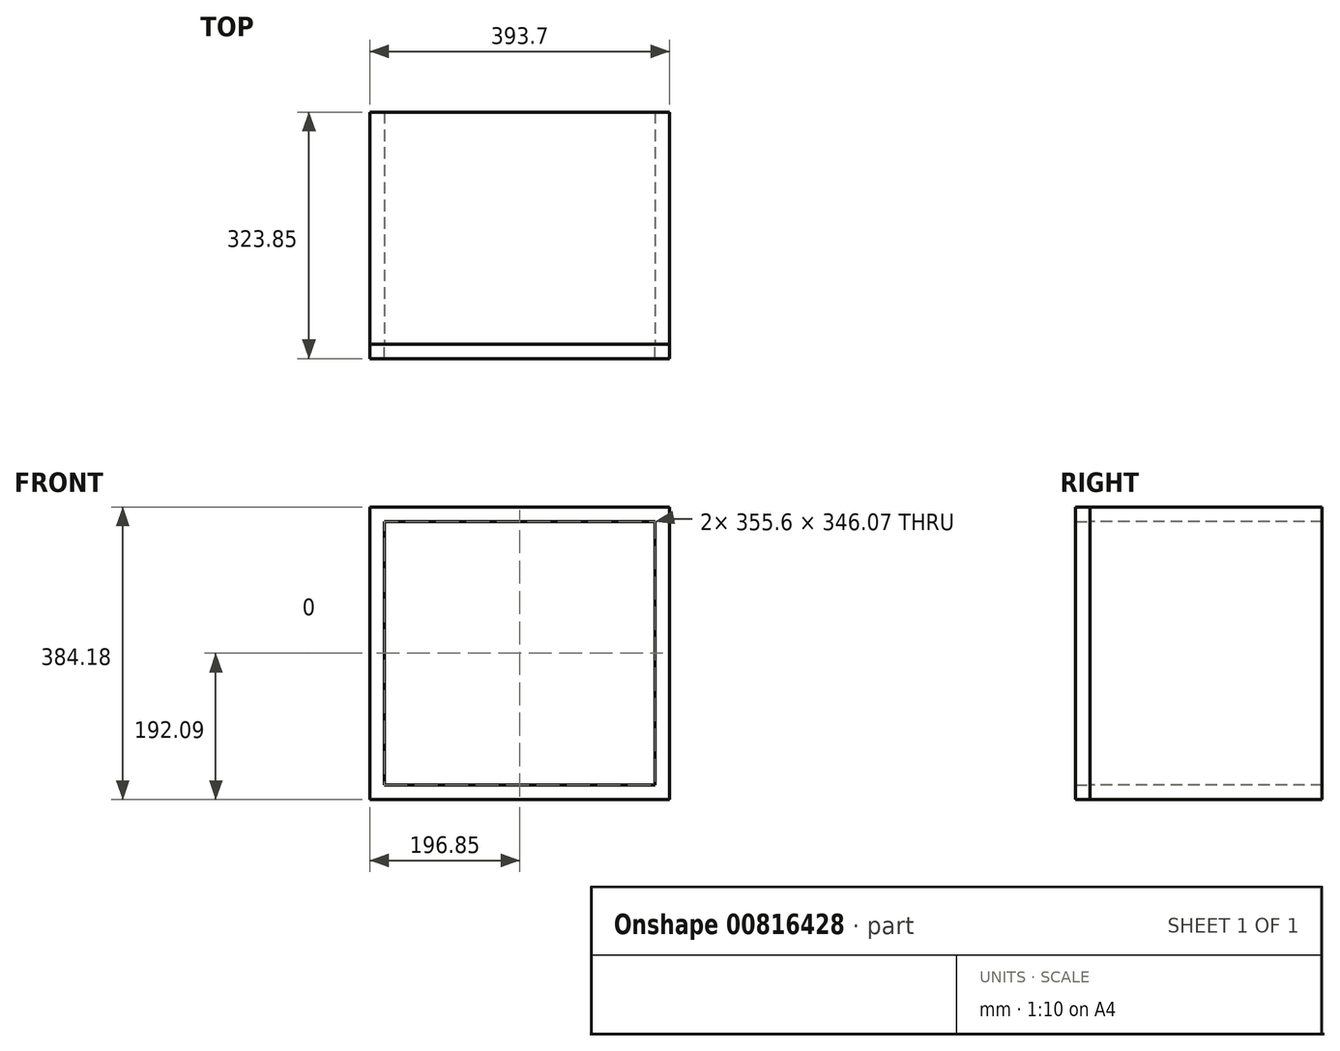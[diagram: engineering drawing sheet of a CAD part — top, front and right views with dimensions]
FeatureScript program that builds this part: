
annotation { "Feature Type Name" : "Feature", "Feature Type Description" : "" }
export const myFeature = defineFeature(function(context is Context, id is Id, definition is map)
    precondition{}
    {
        {
            var Q0;
            Q0=qCreatedBy(makeId("Front.planeOp"),FACE);
            var sketch = newSketch(context, id + "F0", { "sketchPlane" : qUnion([Q0])});
            skLineSegment(sketch, "E0.bottom", {"start": v(196.85, 192.09) * mm, "end": v(-196.85, 192.09) * mm});
            skLineSegment(sketch, "E0.top", {"start": v(196.85, -192.09) * mm, "end": v(-196.85, -192.09) * mm});
            skLineSegment(sketch, "E0.left", {"start": v(196.85, 192.09) * mm, "end": v(196.85, -192.09) * mm});
            skLineSegment(sketch, "E0.right", {"start": v(-196.85, 192.09) * mm, "end": v(-196.85, -192.09) * mm});
            skPoint(sketch, "E0.middle", {"position": v(0, 0) * mm});
            skLineSegment(sketch, "E1.0", {"start": v(-177.8, 173.04) * mm, "end": v(-177.8, -173.04) * mm});
            skLineSegment(sketch, "E1.1", {"start": v(177.8, 173.04) * mm, "end": v(-177.8, 173.04) * mm});
            skLineSegment(sketch, "E1.2", {"start": v(177.8, 173.04) * mm, "end": v(177.8, -173.04) * mm});
            skLineSegment(sketch, "E1.3", {"start": v(177.8, -173.04) * mm, "end": v(-177.8, -173.04) * mm});
            skSolve(sketch);
        }
        {
            var Q0;
            Q0 = qSketchRegion(id + "F0", true);
            extrude(context, id + "F1", {"entities" : qUnion([Q0]), "oppositeDirection" : true, "depth" : 304.8 * mm, "offsetDistance" : 25.4 * mm});
        }
        {
            var Q0;
            Q0=makeQuery(id+"F1.opExtrude","CAP_FACE",FACE,{"disambiguationData":[OSD([sQuery(id+"F0.wireOp",EDGE,"E0.bottom"),sQuery(id+"F0.wireOp",EDGE,"E0.top"),sQuery(id+"F0.wireOp",EDGE,"E0.left"),sQuery(id+"F0.wireOp",EDGE,"E0.right"),sQuery(id+"F0.wireOp",EDGE,"E1.0"),sQuery(id+"F0.wireOp",EDGE,"E1.1"),sQuery(id+"F0.wireOp",EDGE,"E1.2"),sQuery(id+"F0.wireOp",EDGE,"E1.3")])],"isStart":true});
            var sketch = newSketch(context, id + "F2", { "sketchPlane" : qUnion([Q0])});
            skLineSegment(sketch, "E2.0", {"start": v(177.8, 173.04) * mm, "end": v(177.8, -173.04) * mm});
            skLineSegment(sketch, "E3.0", {"start": v(196.85, 192.09) * mm, "end": v(196.85, -192.09) * mm});
            skLineSegment(sketch, "E4.0", {"start": v(177.8, -173.04) * mm, "end": v(-177.8, -173.04) * mm});
            skLineSegment(sketch, "E5.0", {"start": v(196.85, -192.09) * mm, "end": v(-196.85, -192.09) * mm});
            skLineSegment(sketch, "E6.0", {"start": v(177.8, 173.04) * mm, "end": v(-177.8, 173.04) * mm});
            skLineSegment(sketch, "E7.0", {"start": v(196.85, 192.09) * mm, "end": v(-196.85, 192.09) * mm});
            skLineSegment(sketch, "E8.0", {"start": v(-196.85, 192.09) * mm, "end": v(-196.85, -192.09) * mm});
            skLineSegment(sketch, "E9.0", {"start": v(-177.8, 173.04) * mm, "end": v(-177.8, -173.04) * mm});
            skSolve(sketch);
        }
        {
            var Q0;
            Q0 = qSketchRegion(id + "F2", true);
            extrude(context, id + "F3", {"entities" : qUnion([Q0]), "depth" : 19.05 * mm, "offsetDistance" : 25.4 * mm});
        }
    });
